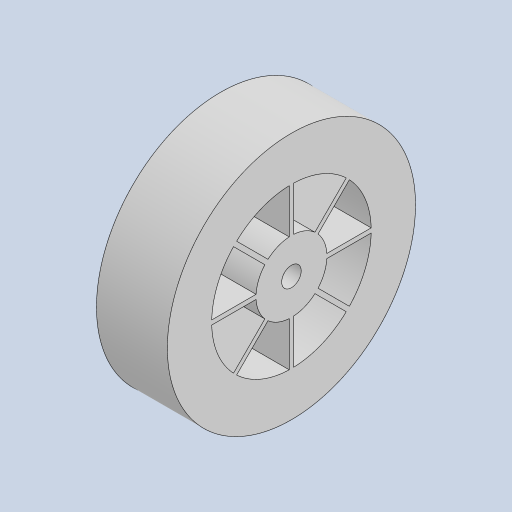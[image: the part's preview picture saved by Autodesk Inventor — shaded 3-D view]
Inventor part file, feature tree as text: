
AUTODESK INVENTOR PART (.ipt)
format: ipt  version: 2023 (Build 270158000, 158)  size: 155,648 bytes
history: native  units: mm
features: sketch x3, extrude x2, other x1, pattern_circular x1, hole x1
ambient origin geometry x8: Origin, YZ Plane, XZ Plane, XY Plane, X Axis, Y Axis, Z Axis, Center Point
bodies: Body1 (feature_tree)
feature tree (8):
  other  "ソリッド1"
  extrude  "押し出し1"  Depth=28.0mm
  extrude  "押し出し2"  Depth=8.0mm TaperAngle=0.0deg
  pattern_circular  "円形状パターン1"  [2 undecoded]
  hole  "穴1"  [1 undecoded]
  sketch  "スケッチ1"
  sketch  "スケッチ2"
  sketch  "スケッチ3"
note: 3 required parameter values undecoded (feature->parameter linkage not recoverable at this tier; creation-order binding heuristic only, values carry confidence <= 0.55)
